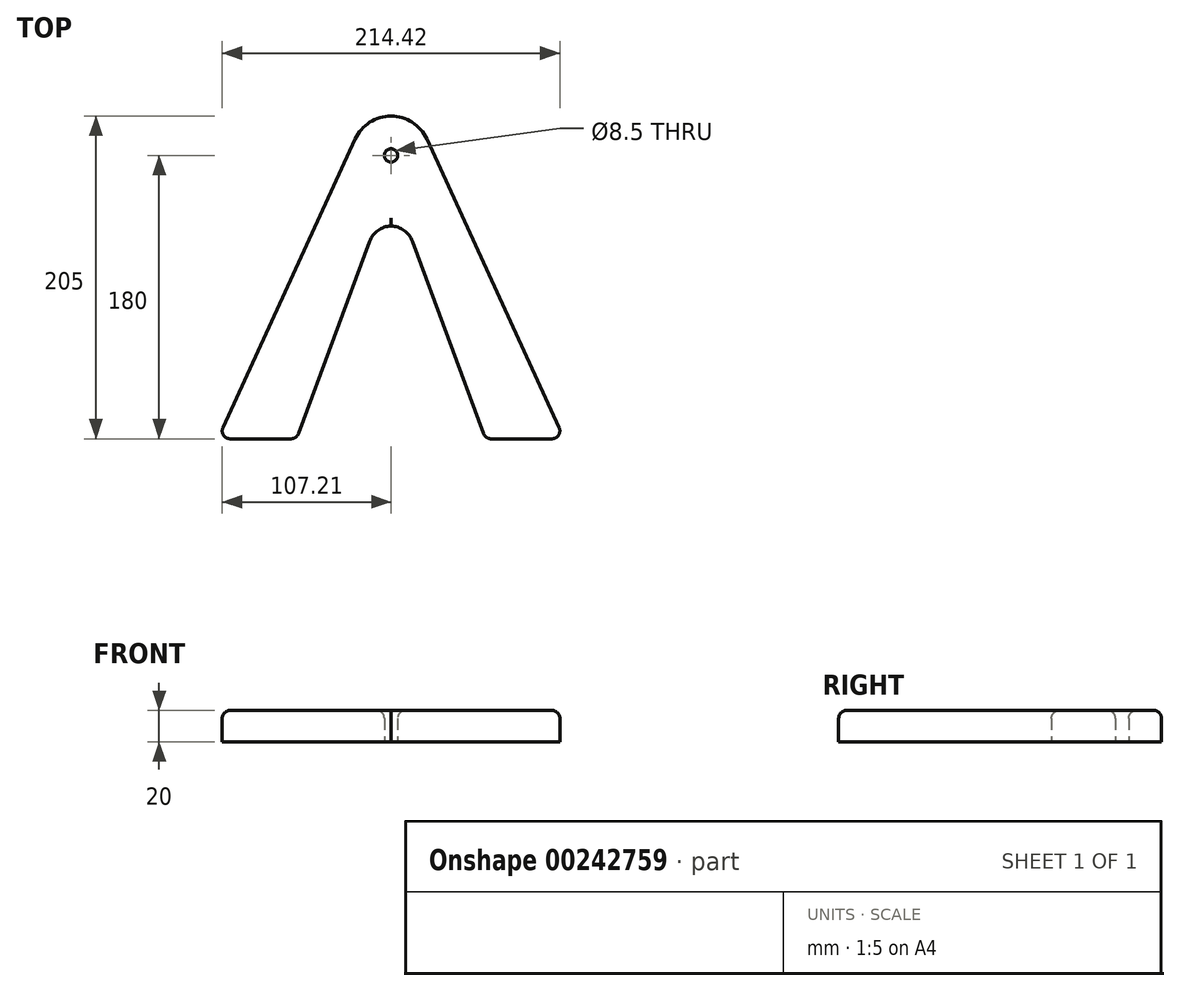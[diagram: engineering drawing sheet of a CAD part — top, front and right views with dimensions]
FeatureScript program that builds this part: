
annotation { "Feature Type Name" : "Feature", "Feature Type Description" : "" }
export const myFeature = defineFeature(function(context is Context, id is Id, definition is map)
    precondition{}
    {
        {
            var Q0;
            Q0=qCreatedBy(makeId("Top.planeOp"),FACE);
            var sketch = newSketch(context, id + "F0", { "sketchPlane" : qUnion([Q0])});
            skCircle(sketch, "E0", {"center": v(0, 0) * mm, "radius": 4.25 * mm});
            skArc(sketch, "E1", {"start": v(0, 25) * mm, "mid": v(-13.5, 21.04) * mm, "end": v(-22.73, 10.42) * mm});
            skLineSegment(sketch, "E2", {"start": v(-110, -180) * mm, "end": v(-22.73, 10.42) * mm});
            skLineSegment(sketch, "E3", {"start": v(-110, -180) * mm, "end": v(-60, -180) * mm});
            skArc(sketch, "E4", {"start": v(0.33, -44.8) * mm, "mid": v(-8.13, -47.53) * mm, "end": v(-13.55, -54.58) * mm});
            skLineSegment(sketch, "E5", {"start": v(-60, -180) * mm, "end": v(-13.55, -54.58) * mm});
            skLineSegment(sketch, "E6", {"start": v(0, 50.53) * mm, "end": v(0, -132.55) * mm, "construction": true});
            skArc(sketch, "E7.MirrorCS", {"start": v(-0.33, -44.8) * mm, "mid": v(8.13, -47.53) * mm, "end": v(13.55, -54.58) * mm});
            skArc(sketch, "E8.MirrorCS", {"start": v(0, 25) * mm, "mid": v(13.5, 21.04) * mm, "end": v(22.73, 10.42) * mm});
            skLineSegment(sketch, "E9.MirrorCS", {"start": v(110, -180) * mm, "end": v(60, -180) * mm});
            skLineSegment(sketch, "E10.MirrorCS", {"start": v(60, -180) * mm, "end": v(13.55, -54.58) * mm});
            skLineSegment(sketch, "E11.MirrorCS", {"start": v(110, -180) * mm, "end": v(22.73, 10.42) * mm});
            skSolve(sketch);
        }
        {
            var Q0;
            Q0 = qSketchRegion(id + "F0", true);
            extrude(context, id + "F1", {"entities" : qUnion([Q0]), "depth" : 20 * mm});
        }
        {
            var Q0;
            Q0=makeQuery(id+"F1.opExtrude","SWEPT_EDGE",EDGE,{"disambiguationData":[OSD([sQuery(id+"F0.wireOp",EDGE,"E2"),sQuery(id+"F0.wireOp",EDGE,"E3")])]});
            var Q1;
            Q1=makeQuery(id+"F1.opExtrude","SWEPT_EDGE",EDGE,{"disambiguationData":[OSD([sQuery(id+"F0.wireOp",EDGE,"E3"),sQuery(id+"F0.wireOp",EDGE,"E5")])]});
            var Q2;
            Q2=makeQuery(id+"F1.opExtrude","SWEPT_EDGE",EDGE,{"disambiguationData":[OSD([sQuery(id+"F0.wireOp",EDGE,"E9.MirrorCS"),sQuery(id+"F0.wireOp",EDGE,"E10.MirrorCS")])]});
            var Q3;
            Q3=makeQuery(id+"F1.opExtrude","SWEPT_EDGE",EDGE,{"disambiguationData":[OSD([sQuery(id+"F0.wireOp",EDGE,"E9.MirrorCS"),sQuery(id+"F0.wireOp",EDGE,"E11.MirrorCS")])]});
            fillet(context, id + "F2", {"entities" : qUnion([Q0, Q1, Q2, Q3]), "radius" : 5 * mm, "tangentPropagation" : true, "allowEdgeOverflow" : false});
        }
        {
            var Q0;
            Q0=makeQuery(id+"F1.opExtrude","CAP_FACE",FACE,{"disambiguationData":[OSD([sQuery(id+"F0.wireOp",EDGE,"E0"),sQuery(id+"F0.wireOp",EDGE,"E1"),sQuery(id+"F0.wireOp",EDGE,"E2"),sQuery(id+"F0.wireOp",EDGE,"E3"),sQuery(id+"F0.wireOp",EDGE,"E4"),sQuery(id+"F0.wireOp",EDGE,"E5"),sQuery(id+"F0.wireOp",EDGE,"E7.MirrorCS"),sQuery(id+"F0.wireOp",EDGE,"E8.MirrorCS"),sQuery(id+"F0.wireOp",EDGE,"E9.MirrorCS"),sQuery(id+"F0.wireOp",EDGE,"E10.MirrorCS"),sQuery(id+"F0.wireOp",EDGE,"E11.MirrorCS")])],"isStart":false});
            fillet(context, id + "F3", {"entities" : qUnion([Q0]), "radius" : 5 * mm, "tangentPropagation" : true, "allowEdgeOverflow" : false});
        }
    });
